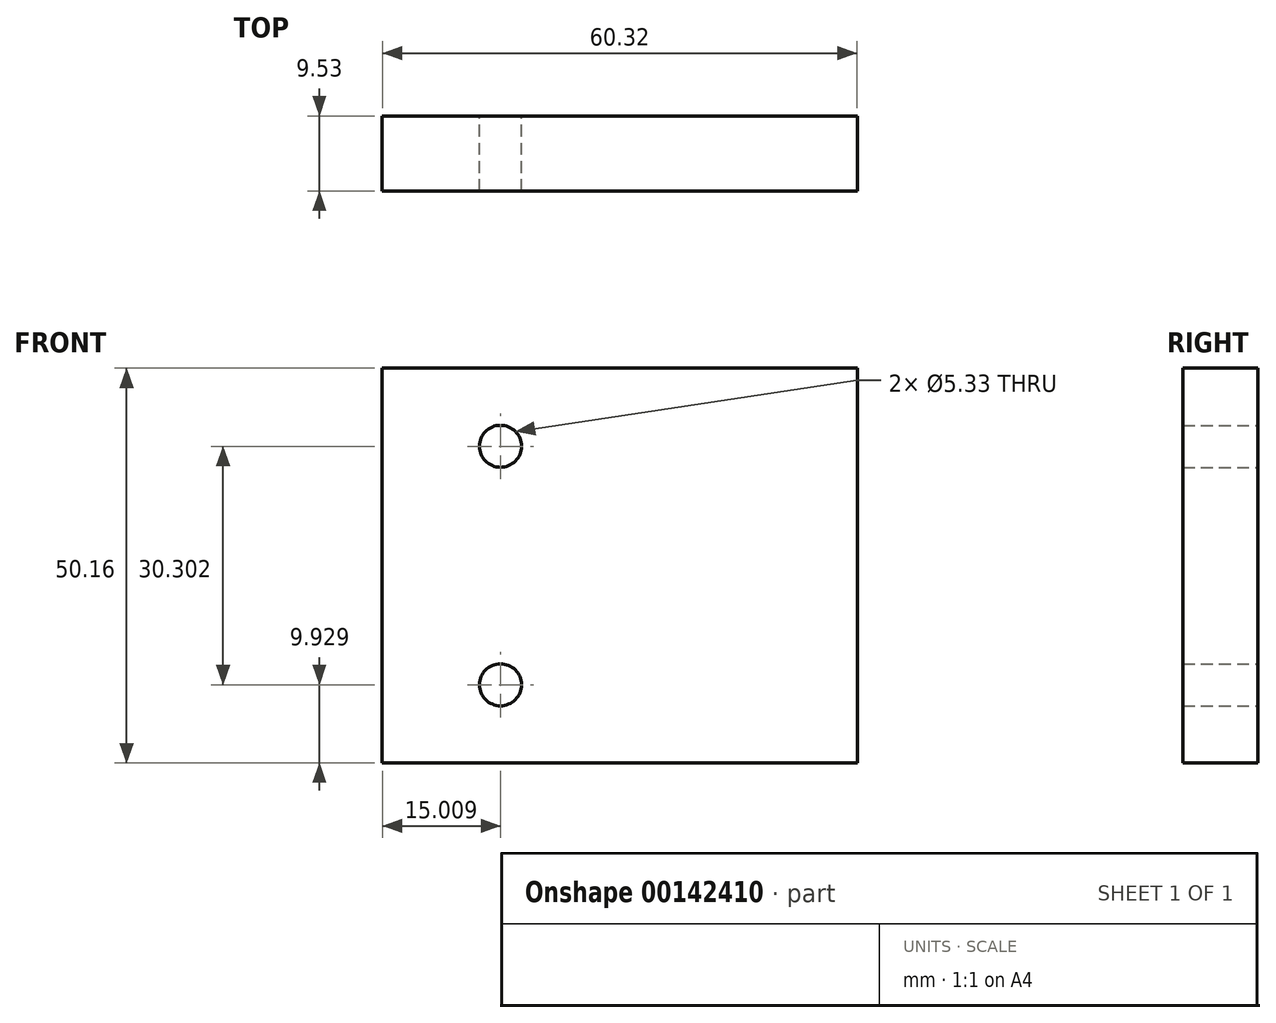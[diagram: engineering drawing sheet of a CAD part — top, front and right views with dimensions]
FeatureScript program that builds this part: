
annotation { "Feature Type Name" : "Feature", "Feature Type Description" : "" }
export const myFeature = defineFeature(function(context is Context, id is Id, definition is map)
    precondition{}
    {
        {
            var Q0;
            Q0=qCreatedBy(makeId("Front.planeOp"),FACE);
            var sketch = newSketch(context, id + "F0", { "sketchPlane" : qUnion([Q0])});
            skLineSegment(sketch, "E0.bottom", {"start": v(30.16, 25.08) * mm, "end": v(-30.16, 25.08) * mm});
            skLineSegment(sketch, "E0.top", {"start": v(30.16, -25.08) * mm, "end": v(-30.16, -25.08) * mm});
            skLineSegment(sketch, "E0.left", {"start": v(30.16, 25.08) * mm, "end": v(30.16, -25.08) * mm});
            skLineSegment(sketch, "E0.right", {"start": v(-30.16, 25.08) * mm, "end": v(-30.16, -25.08) * mm});
            skPoint(sketch, "E0.middle", {"position": v(0, 0) * mm});
            skCircle(sketch, "E1", {"center": v(-15.15, 15.15) * mm, "radius": 2.67 * mm});
            skCircle(sketch, "E2.MirrorC", {"center": v(-15.15, -15.15) * mm, "radius": 2.67 * mm});
            skSolve(sketch);
        }
        {
            var Q0;
            Q0=makeQuery(id+"F0.imprint","IMPRINT",FACE,{"disambiguationData":[TD([[makeQuery(id+"F0.imprint","IMPRINT",EDGE,{"derivedFrom":sQuery(id+"F0.wireOp",EDGE,"E0.bottom")}),1.0]])]});
            extrude(context, id + "F1", {"entities" : qUnion([Q0]), "depth" : 9.52 * mm, "offsetDistance" : 25.4 * mm});
        }
    });
